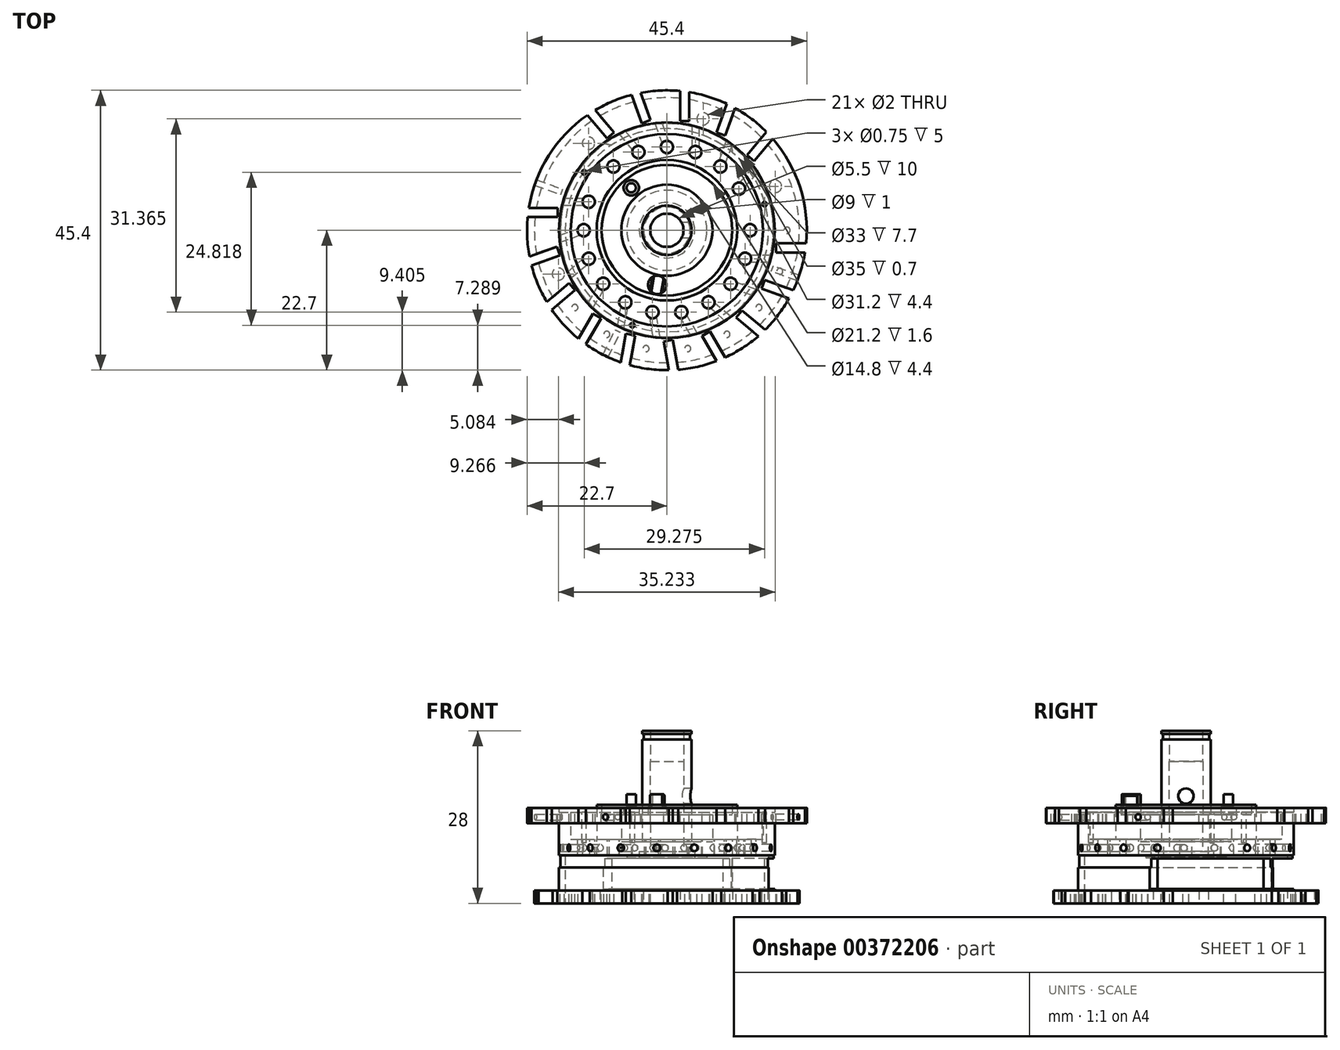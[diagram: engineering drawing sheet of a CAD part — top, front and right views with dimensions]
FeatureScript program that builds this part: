
annotation { "Feature Type Name" : "Feature", "Feature Type Description" : "" }
export const myFeature = defineFeature(function(context is Context, id is Id, definition is map)
    precondition{}
    {
        {
            var Q0;
            Q0=qCreatedBy(makeId("Front.planeOp"),FACE);
            var sketch = newSketch(context, id + "F0", { "sketchPlane" : qUnion([Q0])});
            skLineSegment(sketch, "E0", {"start": v(4, 20.6) * mm, "end": v(4, 20.1) * mm});
            skLineSegment(sketch, "E1", {"start": v(4, 20.1) * mm, "end": v(3.75, 20.1) * mm});
            skLineSegment(sketch, "E2", {"start": v(3.75, 20.1) * mm, "end": v(3.75, 19.2) * mm});
            skLineSegment(sketch, "E3", {"start": v(3.75, 19.2) * mm, "end": v(4, 19.2) * mm});
            skLineSegment(sketch, "E4", {"start": v(4, 19.2) * mm, "end": v(4, 2.6) * mm});
            skLineSegment(sketch, "E5", {"start": v(4, 2.6) * mm, "end": v(7.4, 2.6) * mm});
            skLineSegment(sketch, "E6", {"start": v(7.4, 2.6) * mm, "end": v(7.4, 7) * mm});
            skLineSegment(sketch, "E7", {"start": v(7.4, 7) * mm, "end": v(10.6, 7) * mm});
            skLineSegment(sketch, "E8", {"start": v(10.6, 7) * mm, "end": v(10.6, 8.6) * mm});
            skLineSegment(sketch, "E9", {"start": v(10.6, 8.6) * mm, "end": v(11.4, 8.6) * mm});
            skLineSegment(sketch, "E10", {"start": v(11.4, 8.6) * mm, "end": v(11.4, 3) * mm});
            skLineSegment(sketch, "E11", {"start": v(11.4, 3) * mm, "end": v(15.6, 3) * mm});
            skLineSegment(sketch, "E12", {"start": v(15.6, 3) * mm, "end": v(15.6, 7.4) * mm});
            skLineSegment(sketch, "E13", {"start": v(15.6, 7.4) * mm, "end": v(17.5, 7.4) * mm});
            skLineSegment(sketch, "E14", {"start": v(17.5, 7.4) * mm, "end": v(17.5, 8.1) * mm});
            skLineSegment(sketch, "E15", {"start": v(17.5, 8.1) * mm, "end": v(22.7, 8.1) * mm});
            skLineSegment(sketch, "E16", {"start": v(22.7, 8.1) * mm, "end": v(22.7, 5.6) * mm});
            skLineSegment(sketch, "E17", {"start": v(22.7, 5.6) * mm, "end": v(17.5, 5.6) * mm});
            skLineSegment(sketch, "E18", {"start": v(17.5, 5.6) * mm, "end": v(17.5, 0.4) * mm});
            skLineSegment(sketch, "E19", {"start": v(17.5, 0.4) * mm, "end": v(17.3, 0.4) * mm});
            skLineSegment(sketch, "E20", {"start": v(17.3, 0.4) * mm, "end": v(17.3, -1.6) * mm});
            skLineSegment(sketch, "E21", {"start": v(17.3, -1.6) * mm, "end": v(17.5, -1.6) * mm});
            skLineSegment(sketch, "E22", {"start": v(17.5, -1.6) * mm, "end": v(17.5, -5.3) * mm});
            skLineSegment(sketch, "E23", {"start": v(17.5, -5.3) * mm, "end": v(21.5, -5.3) * mm});
            skLineSegment(sketch, "E24", {"start": v(21.5, -5.3) * mm, "end": v(21.5, -7.4) * mm});
            skLineSegment(sketch, "E25", {"start": v(21.5, -7.4) * mm, "end": v(16.5, -7.4) * mm});
            skLineSegment(sketch, "E26", {"start": v(16.5, -7.4) * mm, "end": v(16.5, 0.3) * mm});
            skLineSegment(sketch, "E27", {"start": v(16.5, 0.3) * mm, "end": v(6.5, 0.3) * mm});
            skLineSegment(sketch, "E28", {"start": v(6.5, 0.3) * mm, "end": v(6.5, 0) * mm});
            skLineSegment(sketch, "E29", {"start": v(6.5, 0) * mm, "end": v(4.5, 0) * mm});
            skLineSegment(sketch, "E30", {"start": v(4.5, 0) * mm, "end": v(4.5, 1) * mm});
            skLineSegment(sketch, "E31", {"start": v(4.5, 1) * mm, "end": v(2.7, 1) * mm});
            skLineSegment(sketch, "E32", {"start": v(2.7, 1) * mm, "end": v(2.7, 5.6) * mm});
            skLineSegment(sketch, "E33", {"start": v(2.7, 5.6) * mm, "end": v(2.75, 5.6) * mm});
            skLineSegment(sketch, "E34", {"start": v(2.75, 5.6) * mm, "end": v(2.75, 15.6) * mm});
            skLineSegment(sketch, "E35", {"start": v(2.75, 15.6) * mm, "end": v(2.7, 15.6) * mm});
            skLineSegment(sketch, "E36", {"start": v(2.7, 15.6) * mm, "end": v(2.7, 20.6) * mm});
            skLineSegment(sketch, "E37", {"start": v(2.7, 20.6) * mm, "end": v(4, 20.6) * mm});
            skLineSegment(sketch, "E38", {"start": v(0, 0) * mm, "end": v(0, 20.6) * mm, "construction": true});
            skSolve(sketch);
        }
        {
            var Q0;
            Q0=makeQuery(id+"F0.imprint","IMPRINT",FACE,{"disambiguationData":[TD([[makeQuery(id+"F0.imprint","IMPRINT",EDGE,{"derivedFrom":sQuery(id+"F0.wireOp",EDGE,"E0")}),-1.0]])]});
            var Q1;
            Q1=sQuery(id+"F0.wireOp",EDGE,"E38");
            revolve(context, id + "F1", {"entities" : qUnion([Q0]), "axis" : qUnion([Q1]), "revolveType" : RevolveType.FULL});
        }
        {
            var Q0;
            Q0=makeQuery(id+"F1.opRevolve","SWEPT_FACE",FACE,{"disambiguationData":[OSD([sQuery(id+"F0.wireOp",EDGE,"E15")])]});
            var sketch = newSketch(context, id + "F2", { "sketchPlane" : qUnion([Q0])});
            skLineSegment(sketch, "E39.bottom", {"start": v(24.7, -2.13) * mm, "end": v(17.7, -2.13) * mm});
            skLineSegment(sketch, "E39.top", {"start": v(24.7, -3.63) * mm, "end": v(17.7, -3.63) * mm});
            skLineSegment(sketch, "E39.left", {"start": v(24.7, -2.13) * mm, "end": v(24.7, -3.63) * mm});
            skLineSegment(sketch, "E39.right", {"start": v(17.7, -2.13) * mm, "end": v(17.7, -3.63) * mm});
            skLineSegment(sketch, "E40", {"start": v(14.9, -4.63) * mm, "end": v(24.7, -4.63) * mm, "construction": true});
            skLineSegment(sketch, "E41", {"start": v(0, 0) * mm, "end": v(21.33, -7.76) * mm, "construction": true});
            skPoint(sketch, "E42", {"position": v(12.69, -4.62) * mm});
            skCircle(sketch, "E43", {"center": v(12.69, -4.62) * mm, "radius": 1 * mm});
            skLineSegment(sketch, "E44", {"start": v(14.9, -4.63) * mm, "end": v(13.69, -4.63) * mm, "construction": true});
            skSolve(sketch);
        }
        {
            var Q0;
            Q0=makeQuery(id+"F2.imprint","IMPRINT",FACE,{"disambiguationData":[TD([[makeQuery(id+"F2.imprint","IMPRINT",EDGE,{"derivedFrom":sQuery(id+"F2.wireOp",EDGE,"E43")}),1.0]])]});
            var Q1;
            {var subQ5=sQuery(id+"F2.wireOp",EDGE,"E39.right");Q1=makeQuery(id+"F2.imprint","IMPRINT",FACE,{"disambiguationData":[TD([[makeQuery(id+"F2.imprint","IMPRINT",EDGE,{"derivedFrom":subQ5}),1.0]])]});}
            extrude(context, id + "F3", {"entities" : qUnion([Q0, Q1]), "oppositeDirection" : true, "depth" : 16 * mm});
        }
        {
            var Q0;
            Q0=makeQuery(id+"F3.opExtrude","SWEPT_BODY",BODY,{"disambiguationData":[OSD([sQuery(id+"F0.wireOp",EDGE,"E15"),sQuery(id+"F0.wireOp",EDGE,"E16"),sQuery(id+"F2.wireOp",EDGE,"E39.bottom"),sQuery(id+"F2.wireOp",EDGE,"E39.top"),sQuery(id+"F2.wireOp",EDGE,"E39.right")])]});
            var Q1;
            Q1=makeQuery(id+"F3.opExtrude","SWEPT_BODY",BODY,{"disambiguationData":[OSD([sQuery(id+"F2.wireOp",EDGE,"E43")])]});
            var Q2;
            Q2=sQuery(id+"F0.wireOp",EDGE,"E38");
            circularPattern(context, id + "F4", {"entities" : qUnion([Q0, Q1]), "axis" : qUnion([Q2]), "angle" : 20 * degree, "instanceCount" : round(10), "oppositeDirection" : true, "computeTransformsWithoutBuiltin" : true});
        }
        {
            var Q0;
            Q0=makeQuery(id+"F3.opExtrude","SWEPT_BODY",BODY,{"disambiguationData":[OSD([sQuery(id+"F0.wireOp",EDGE,"E15"),sQuery(id+"F0.wireOp",EDGE,"E16"),sQuery(id+"F2.wireOp",EDGE,"E39.bottom"),sQuery(id+"F2.wireOp",EDGE,"E39.top"),sQuery(id+"F2.wireOp",EDGE,"E39.right")])]});
            var Q1;
            Q1=makeQuery(id+"F3.opExtrude","SWEPT_BODY",BODY,{"disambiguationData":[OSD([sQuery(id+"F2.wireOp",EDGE,"E43")])]});
            var Q2;
            Q2=sQuery(id+"F0.wireOp",EDGE,"E38");
            circularPattern(context, id + "F5", {"entities" : qUnion([Q0, Q1]), "axis" : qUnion([Q2]), "angle" : 50 * degree, "instanceCount" : round(2), "computeTransformsWithoutBuiltin" : true});
        }
        {
            var Q0;
            Q0=makeQuery(id+"F5.opPattern","COPY",BODY,{"derivedFrom":makeQuery(id+"F3.opExtrude","SWEPT_BODY",BODY,{"disambiguationData":[OSD([sQuery(id+"F2.wireOp",EDGE,"E43")])]}),"instanceName":"1"});
            var Q1;
            Q1=makeQuery(id+"F5.opPattern","COPY",BODY,{"derivedFrom":makeQuery(id+"F3.opExtrude","SWEPT_BODY",BODY,{"disambiguationData":[OSD([sQuery(id+"F0.wireOp",EDGE,"E15"),sQuery(id+"F0.wireOp",EDGE,"E16"),sQuery(id+"F2.wireOp",EDGE,"E39.bottom"),sQuery(id+"F2.wireOp",EDGE,"E39.top"),sQuery(id+"F2.wireOp",EDGE,"E39.right")])]}),"instanceName":"1"});
            var Q2;
            Q2=sQuery(id+"F0.wireOp",EDGE,"E38");
            circularPattern(context, id + "F6", {"entities" : qUnion([Q0, Q1]), "axis" : qUnion([Q2]), "angle" : 20 * degree, "instanceCount" : round(5), "computeTransformsWithoutBuiltin" : true});
        }
        {
            var Q0;
            Q0=makeQuery(id+"F6.opPattern","COPY",BODY,{"derivedFrom":makeQuery(id+"F5.opPattern","COPY",BODY,{"derivedFrom":makeQuery(id+"F3.opExtrude","SWEPT_BODY",BODY,{"disambiguationData":[OSD([sQuery(id+"F2.wireOp",EDGE,"E43")])]}),"instanceName":"1"}),"instanceName":"4"});
            var Q1;
            Q1=sQuery(id+"F0.wireOp",EDGE,"E38");
            transform(context, id + "F7", {"entities" : qUnion([Q0]), "transformType" : TransformType.ROTATION, "transformAxis" : qUnion([Q1]), "angle" : 20 * degree, "makeCopy" : true});
        }
        {
            var Q0;
            Q0=makeQuery(id+"F3.opExtrude","SWEPT_BODY",BODY,{"disambiguationData":[OSD([sQuery(id+"F0.wireOp",EDGE,"E15"),sQuery(id+"F0.wireOp",EDGE,"E16"),sQuery(id+"F2.wireOp",EDGE,"E39.bottom"),sQuery(id+"F2.wireOp",EDGE,"E39.top"),sQuery(id+"F2.wireOp",EDGE,"E39.right")])]});
            var Q1;
            Q1=makeQuery(id+"F3.opExtrude","SWEPT_BODY",BODY,{"disambiguationData":[OSD([sQuery(id+"F2.wireOp",EDGE,"E43")])]});
            var Q2;
            Q2=makeQuery(id+"F4.opPattern","COPY",BODY,{"derivedFrom":makeQuery(id+"F3.opExtrude","SWEPT_BODY",BODY,{"disambiguationData":[OSD([sQuery(id+"F0.wireOp",EDGE,"E15"),sQuery(id+"F0.wireOp",EDGE,"E16"),sQuery(id+"F2.wireOp",EDGE,"E39.bottom"),sQuery(id+"F2.wireOp",EDGE,"E39.top"),sQuery(id+"F2.wireOp",EDGE,"E39.right")])]}),"instanceName":"1"});
            var Q3;
            Q3=makeQuery(id+"F4.opPattern","COPY",BODY,{"derivedFrom":makeQuery(id+"F3.opExtrude","SWEPT_BODY",BODY,{"disambiguationData":[OSD([sQuery(id+"F2.wireOp",EDGE,"E43")])]}),"instanceName":"1"});
            var Q4;
            Q4=makeQuery(id+"F4.opPattern","COPY",BODY,{"derivedFrom":makeQuery(id+"F3.opExtrude","SWEPT_BODY",BODY,{"disambiguationData":[OSD([sQuery(id+"F0.wireOp",EDGE,"E15"),sQuery(id+"F0.wireOp",EDGE,"E16"),sQuery(id+"F2.wireOp",EDGE,"E39.bottom"),sQuery(id+"F2.wireOp",EDGE,"E39.top"),sQuery(id+"F2.wireOp",EDGE,"E39.right")])]}),"instanceName":"2"});
            var Q5;
            Q5=makeQuery(id+"F4.opPattern","COPY",BODY,{"derivedFrom":makeQuery(id+"F3.opExtrude","SWEPT_BODY",BODY,{"disambiguationData":[OSD([sQuery(id+"F2.wireOp",EDGE,"E43")])]}),"instanceName":"2"});
            var Q6;
            Q6=makeQuery(id+"F4.opPattern","COPY",BODY,{"derivedFrom":makeQuery(id+"F3.opExtrude","SWEPT_BODY",BODY,{"disambiguationData":[OSD([sQuery(id+"F0.wireOp",EDGE,"E15"),sQuery(id+"F0.wireOp",EDGE,"E16"),sQuery(id+"F2.wireOp",EDGE,"E39.bottom"),sQuery(id+"F2.wireOp",EDGE,"E39.top"),sQuery(id+"F2.wireOp",EDGE,"E39.right")])]}),"instanceName":"3"});
            var Q7;
            Q7=makeQuery(id+"F4.opPattern","COPY",BODY,{"derivedFrom":makeQuery(id+"F3.opExtrude","SWEPT_BODY",BODY,{"disambiguationData":[OSD([sQuery(id+"F2.wireOp",EDGE,"E43")])]}),"instanceName":"3"});
            var Q8;
            Q8=makeQuery(id+"F4.opPattern","COPY",BODY,{"derivedFrom":makeQuery(id+"F3.opExtrude","SWEPT_BODY",BODY,{"disambiguationData":[OSD([sQuery(id+"F0.wireOp",EDGE,"E15"),sQuery(id+"F0.wireOp",EDGE,"E16"),sQuery(id+"F2.wireOp",EDGE,"E39.bottom"),sQuery(id+"F2.wireOp",EDGE,"E39.top"),sQuery(id+"F2.wireOp",EDGE,"E39.right")])]}),"instanceName":"4"});
            var Q9;
            Q9=makeQuery(id+"F4.opPattern","COPY",BODY,{"derivedFrom":makeQuery(id+"F3.opExtrude","SWEPT_BODY",BODY,{"disambiguationData":[OSD([sQuery(id+"F2.wireOp",EDGE,"E43")])]}),"instanceName":"4"});
            var Q10;
            Q10=makeQuery(id+"F4.opPattern","COPY",BODY,{"derivedFrom":makeQuery(id+"F3.opExtrude","SWEPT_BODY",BODY,{"disambiguationData":[OSD([sQuery(id+"F0.wireOp",EDGE,"E15"),sQuery(id+"F0.wireOp",EDGE,"E16"),sQuery(id+"F2.wireOp",EDGE,"E39.bottom"),sQuery(id+"F2.wireOp",EDGE,"E39.top"),sQuery(id+"F2.wireOp",EDGE,"E39.right")])]}),"instanceName":"5"});
            var Q11;
            Q11=makeQuery(id+"F4.opPattern","COPY",BODY,{"derivedFrom":makeQuery(id+"F3.opExtrude","SWEPT_BODY",BODY,{"disambiguationData":[OSD([sQuery(id+"F2.wireOp",EDGE,"E43")])]}),"instanceName":"5"});
            var Q12;
            Q12=makeQuery(id+"F4.opPattern","COPY",BODY,{"derivedFrom":makeQuery(id+"F3.opExtrude","SWEPT_BODY",BODY,{"disambiguationData":[OSD([sQuery(id+"F0.wireOp",EDGE,"E15"),sQuery(id+"F0.wireOp",EDGE,"E16"),sQuery(id+"F2.wireOp",EDGE,"E39.bottom"),sQuery(id+"F2.wireOp",EDGE,"E39.top"),sQuery(id+"F2.wireOp",EDGE,"E39.right")])]}),"instanceName":"6"});
            var Q13;
            Q13=makeQuery(id+"F4.opPattern","COPY",BODY,{"derivedFrom":makeQuery(id+"F3.opExtrude","SWEPT_BODY",BODY,{"disambiguationData":[OSD([sQuery(id+"F2.wireOp",EDGE,"E43")])]}),"instanceName":"6"});
            var Q14;
            Q14=makeQuery(id+"F4.opPattern","COPY",BODY,{"derivedFrom":makeQuery(id+"F3.opExtrude","SWEPT_BODY",BODY,{"disambiguationData":[OSD([sQuery(id+"F0.wireOp",EDGE,"E15"),sQuery(id+"F0.wireOp",EDGE,"E16"),sQuery(id+"F2.wireOp",EDGE,"E39.bottom"),sQuery(id+"F2.wireOp",EDGE,"E39.top"),sQuery(id+"F2.wireOp",EDGE,"E39.right")])]}),"instanceName":"7"});
            var Q15;
            Q15=makeQuery(id+"F4.opPattern","COPY",BODY,{"derivedFrom":makeQuery(id+"F3.opExtrude","SWEPT_BODY",BODY,{"disambiguationData":[OSD([sQuery(id+"F2.wireOp",EDGE,"E43")])]}),"instanceName":"7"});
            var Q16;
            Q16=makeQuery(id+"F4.opPattern","COPY",BODY,{"derivedFrom":makeQuery(id+"F3.opExtrude","SWEPT_BODY",BODY,{"disambiguationData":[OSD([sQuery(id+"F0.wireOp",EDGE,"E15"),sQuery(id+"F0.wireOp",EDGE,"E16"),sQuery(id+"F2.wireOp",EDGE,"E39.bottom"),sQuery(id+"F2.wireOp",EDGE,"E39.top"),sQuery(id+"F2.wireOp",EDGE,"E39.right")])]}),"instanceName":"8"});
            var Q17;
            Q17=makeQuery(id+"F4.opPattern","COPY",BODY,{"derivedFrom":makeQuery(id+"F3.opExtrude","SWEPT_BODY",BODY,{"disambiguationData":[OSD([sQuery(id+"F2.wireOp",EDGE,"E43")])]}),"instanceName":"8"});
            var Q18;
            Q18=makeQuery(id+"F4.opPattern","COPY",BODY,{"derivedFrom":makeQuery(id+"F3.opExtrude","SWEPT_BODY",BODY,{"disambiguationData":[OSD([sQuery(id+"F0.wireOp",EDGE,"E15"),sQuery(id+"F0.wireOp",EDGE,"E16"),sQuery(id+"F2.wireOp",EDGE,"E39.bottom"),sQuery(id+"F2.wireOp",EDGE,"E39.top"),sQuery(id+"F2.wireOp",EDGE,"E39.right")])]}),"instanceName":"9"});
            var Q19;
            Q19=makeQuery(id+"F4.opPattern","COPY",BODY,{"derivedFrom":makeQuery(id+"F3.opExtrude","SWEPT_BODY",BODY,{"disambiguationData":[OSD([sQuery(id+"F2.wireOp",EDGE,"E43")])]}),"instanceName":"9"});
            var Q20;
            Q20=makeQuery(id+"F5.opPattern","COPY",BODY,{"derivedFrom":makeQuery(id+"F3.opExtrude","SWEPT_BODY",BODY,{"disambiguationData":[OSD([sQuery(id+"F0.wireOp",EDGE,"E15"),sQuery(id+"F0.wireOp",EDGE,"E16"),sQuery(id+"F2.wireOp",EDGE,"E39.bottom"),sQuery(id+"F2.wireOp",EDGE,"E39.top"),sQuery(id+"F2.wireOp",EDGE,"E39.right")])]}),"instanceName":"1"});
            var Q21;
            Q21=makeQuery(id+"F5.opPattern","COPY",BODY,{"derivedFrom":makeQuery(id+"F3.opExtrude","SWEPT_BODY",BODY,{"disambiguationData":[OSD([sQuery(id+"F2.wireOp",EDGE,"E43")])]}),"instanceName":"1"});
            var Q22;
            Q22=makeQuery(id+"F6.opPattern","COPY",BODY,{"derivedFrom":makeQuery(id+"F5.opPattern","COPY",BODY,{"derivedFrom":makeQuery(id+"F3.opExtrude","SWEPT_BODY",BODY,{"disambiguationData":[OSD([sQuery(id+"F0.wireOp",EDGE,"E15"),sQuery(id+"F0.wireOp",EDGE,"E16"),sQuery(id+"F2.wireOp",EDGE,"E39.bottom"),sQuery(id+"F2.wireOp",EDGE,"E39.top"),sQuery(id+"F2.wireOp",EDGE,"E39.right")])]}),"instanceName":"1"}),"instanceName":"1"});
            var Q23;
            Q23=makeQuery(id+"F6.opPattern","COPY",BODY,{"derivedFrom":makeQuery(id+"F5.opPattern","COPY",BODY,{"derivedFrom":makeQuery(id+"F3.opExtrude","SWEPT_BODY",BODY,{"disambiguationData":[OSD([sQuery(id+"F2.wireOp",EDGE,"E43")])]}),"instanceName":"1"}),"instanceName":"1"});
            var Q24;
            Q24=makeQuery(id+"F6.opPattern","COPY",BODY,{"derivedFrom":makeQuery(id+"F5.opPattern","COPY",BODY,{"derivedFrom":makeQuery(id+"F3.opExtrude","SWEPT_BODY",BODY,{"disambiguationData":[OSD([sQuery(id+"F0.wireOp",EDGE,"E15"),sQuery(id+"F0.wireOp",EDGE,"E16"),sQuery(id+"F2.wireOp",EDGE,"E39.bottom"),sQuery(id+"F2.wireOp",EDGE,"E39.top"),sQuery(id+"F2.wireOp",EDGE,"E39.right")])]}),"instanceName":"1"}),"instanceName":"2"});
            var Q25;
            Q25=makeQuery(id+"F6.opPattern","COPY",BODY,{"derivedFrom":makeQuery(id+"F5.opPattern","COPY",BODY,{"derivedFrom":makeQuery(id+"F3.opExtrude","SWEPT_BODY",BODY,{"disambiguationData":[OSD([sQuery(id+"F2.wireOp",EDGE,"E43")])]}),"instanceName":"1"}),"instanceName":"2"});
            var Q26;
            Q26=makeQuery(id+"F6.opPattern","COPY",BODY,{"derivedFrom":makeQuery(id+"F5.opPattern","COPY",BODY,{"derivedFrom":makeQuery(id+"F3.opExtrude","SWEPT_BODY",BODY,{"disambiguationData":[OSD([sQuery(id+"F0.wireOp",EDGE,"E15"),sQuery(id+"F0.wireOp",EDGE,"E16"),sQuery(id+"F2.wireOp",EDGE,"E39.bottom"),sQuery(id+"F2.wireOp",EDGE,"E39.top"),sQuery(id+"F2.wireOp",EDGE,"E39.right")])]}),"instanceName":"1"}),"instanceName":"3"});
            var Q27;
            Q27=makeQuery(id+"F6.opPattern","COPY",BODY,{"derivedFrom":makeQuery(id+"F5.opPattern","COPY",BODY,{"derivedFrom":makeQuery(id+"F3.opExtrude","SWEPT_BODY",BODY,{"disambiguationData":[OSD([sQuery(id+"F2.wireOp",EDGE,"E43")])]}),"instanceName":"1"}),"instanceName":"3"});
            var Q28;
            Q28=makeQuery(id+"F6.opPattern","COPY",BODY,{"derivedFrom":makeQuery(id+"F5.opPattern","COPY",BODY,{"derivedFrom":makeQuery(id+"F3.opExtrude","SWEPT_BODY",BODY,{"disambiguationData":[OSD([sQuery(id+"F0.wireOp",EDGE,"E15"),sQuery(id+"F0.wireOp",EDGE,"E16"),sQuery(id+"F2.wireOp",EDGE,"E39.bottom"),sQuery(id+"F2.wireOp",EDGE,"E39.top"),sQuery(id+"F2.wireOp",EDGE,"E39.right")])]}),"instanceName":"1"}),"instanceName":"4"});
            var Q29;
            Q29=makeQuery(id+"F6.opPattern","COPY",BODY,{"derivedFrom":makeQuery(id+"F5.opPattern","COPY",BODY,{"derivedFrom":makeQuery(id+"F3.opExtrude","SWEPT_BODY",BODY,{"disambiguationData":[OSD([sQuery(id+"F2.wireOp",EDGE,"E43")])]}),"instanceName":"1"}),"instanceName":"4"});
            var Q30;
            Q30=makeQuery(id+"F6.opPattern","COPY",BODY,{"derivedFrom":makeQuery(id+"F5.opPattern","COPY",BODY,{"derivedFrom":makeQuery(id+"F3.opExtrude","SWEPT_BODY",BODY,{"disambiguationData":[OSD([sQuery(id+"F0.wireOp",EDGE,"E15"),sQuery(id+"F0.wireOp",EDGE,"E16"),sQuery(id+"F2.wireOp",EDGE,"E39.bottom"),sQuery(id+"F2.wireOp",EDGE,"E39.top"),sQuery(id+"F2.wireOp",EDGE,"E39.right")])]}),"instanceName":"1"}),"instanceName":"5"});
            var Q31;
            Q31=makeQuery(id+"F6.opPattern","COPY",BODY,{"derivedFrom":makeQuery(id+"F5.opPattern","COPY",BODY,{"derivedFrom":makeQuery(id+"F3.opExtrude","SWEPT_BODY",BODY,{"disambiguationData":[OSD([sQuery(id+"F2.wireOp",EDGE,"E43")])]}),"instanceName":"1"}),"instanceName":"5"});
            var Q32;
            Q32=makeQuery(id+"F7.opPattern","COPY",BODY,{"derivedFrom":makeQuery(id+"F6.opPattern","COPY",BODY,{"derivedFrom":makeQuery(id+"F5.opPattern","COPY",BODY,{"derivedFrom":makeQuery(id+"F3.opExtrude","SWEPT_BODY",BODY,{"disambiguationData":[OSD([sQuery(id+"F2.wireOp",EDGE,"E43")])]}),"instanceName":"1"}),"instanceName":"4"}),"instanceName":"1"});
            var Q33;
            Q33=makeQuery(id+"F1.opRevolve","SWEPT_BODY",BODY,{"disambiguationData":[OSD([sQuery(id+"F0.wireOp",EDGE,"E0"),sQuery(id+"F0.wireOp",EDGE,"E1"),sQuery(id+"F0.wireOp",EDGE,"E2"),sQuery(id+"F0.wireOp",EDGE,"E3"),sQuery(id+"F0.wireOp",EDGE,"E4"),sQuery(id+"F0.wireOp",EDGE,"E5"),sQuery(id+"F0.wireOp",EDGE,"E6"),sQuery(id+"F0.wireOp",EDGE,"E7"),sQuery(id+"F0.wireOp",EDGE,"E8"),sQuery(id+"F0.wireOp",EDGE,"E9"),sQuery(id+"F0.wireOp",EDGE,"E10"),sQuery(id+"F0.wireOp",EDGE,"E11"),sQuery(id+"F0.wireOp",EDGE,"E12"),sQuery(id+"F0.wireOp",EDGE,"E13"),sQuery(id+"F0.wireOp",EDGE,"E14"),sQuery(id+"F0.wireOp",EDGE,"E15"),sQuery(id+"F0.wireOp",EDGE,"E16"),sQuery(id+"F0.wireOp",EDGE,"E17"),sQuery(id+"F0.wireOp",EDGE,"E18"),sQuery(id+"F0.wireOp",EDGE,"E19"),sQuery(id+"F0.wireOp",EDGE,"E20"),sQuery(id+"F0.wireOp",EDGE,"E21"),sQuery(id+"F0.wireOp",EDGE,"E22"),sQuery(id+"F0.wireOp",EDGE,"E23"),sQuery(id+"F0.wireOp",EDGE,"E24"),sQuery(id+"F0.wireOp",EDGE,"E25"),sQuery(id+"F0.wireOp",EDGE,"E26"),sQuery(id+"F0.wireOp",EDGE,"E27"),sQuery(id+"F0.wireOp",EDGE,"E28"),sQuery(id+"F0.wireOp",EDGE,"E29"),sQuery(id+"F0.wireOp",EDGE,"E30"),sQuery(id+"F0.wireOp",EDGE,"E31"),sQuery(id+"F0.wireOp",EDGE,"E32"),sQuery(id+"F0.wireOp",EDGE,"E33"),sQuery(id+"F0.wireOp",EDGE,"E34"),sQuery(id+"F0.wireOp",EDGE,"E35"),sQuery(id+"F0.wireOp",EDGE,"E36"),sQuery(id+"F0.wireOp",EDGE,"E37")])]});
            booleanBodies(context, id + "F8", {"operationType" : BooleanOperationType.SUBTRACTION, "tools" : qUnion([Q0, Q1, Q2, Q3, Q4, Q5, Q6, Q7, Q8, Q9, Q10, Q11, Q12, Q13, Q14, Q15, Q16, Q17, Q18, Q19, Q20, Q21, Q22, Q23, Q24, Q25, Q26, Q27, Q28, Q29, Q30, Q31, Q32]), "targets" : qUnion([Q33])});
        }
        {
            var Q0;
            Q0=makeQuery(id+"F1.opRevolve","SWEPT_FACE",FACE,{"disambiguationData":[OSD([sQuery(id+"F0.wireOp",EDGE,"E9")])]});
            cPlane(context, id + "F9", {"entities" : qUnion([Q0]), "cplaneType" : CPlaneType.OFFSET, "offset" : 7 * mm, "oppositeDirection" : true, "width" : 150 * mm, "height" : 150 * mm});
        }
        {
            var Q0;
            Q0=qCreatedBy(id+"F9.planeOp",FACE);
            var sketch = newSketch(context, id + "F10", { "sketchPlane" : qUnion([Q0])});
            skLineSegment(sketch, "E45", {"start": v(23.53, -4.63) * mm, "end": v(13.53, -4.63) * mm, "construction": true});
            skLineSegment(sketch, "E46", {"start": v(0, 0) * mm, "end": v(12.69, -4.62) * mm, "construction": true});
            skCircle(sketch, "E47", {"center": v(12.69, -4.62) * mm, "radius": 1 * mm, "construction": true});
            skLineSegment(sketch, "E48.bottom", {"start": v(13.53, -4.63) * mm, "end": v(23.53, -4.63) * mm});
            skLineSegment(sketch, "E48.top", {"start": v(13.53, -4.08) * mm, "end": v(23.53, -4.08) * mm});
            skLineSegment(sketch, "E48.left", {"start": v(13.53, -4.63) * mm, "end": v(13.53, -4.08) * mm});
            skLineSegment(sketch, "E48.right", {"start": v(23.53, -4.63) * mm, "end": v(23.53, -4.08) * mm});
            skSolve(sketch);
        }
        {
            var Q0;
            Q0=makeQuery(id+"F10.imprint","IMPRINT",FACE,{"disambiguationData":[TD([[makeQuery(id+"F10.imprint","IMPRINT",EDGE,{"derivedFrom":sQuery(id+"F10.wireOp",EDGE,"E48.bottom")}),1.0]])]});
            var Q1;
            Q1=sQuery(id+"F10.wireOp",EDGE,"E48.bottom");
            revolve(context, id + "F11", {"entities" : qUnion([Q0]), "axis" : qUnion([Q1]), "revolveType" : RevolveType.FULL});
        }
        {
            var Q0;
            Q0=makeQuery(id+"F11.opRevolve","SWEPT_BODY",BODY,{"disambiguationData":[OSD([sQuery(id+"F10.wireOp",EDGE,"E48.bottom"),sQuery(id+"F10.wireOp",EDGE,"E48.top"),sQuery(id+"F10.wireOp",EDGE,"E48.left"),sQuery(id+"F10.wireOp",EDGE,"E48.right")])]});
            var Q1;
            Q1=sQuery(id+"F0.wireOp",EDGE,"E38");
            circularPattern(context, id + "F12", {"entities" : qUnion([Q0]), "axis" : qUnion([Q1]), "angle" : 20 * degree, "instanceCount" : round(10), "oppositeDirection" : true, "computeTransformsWithoutBuiltin" : true});
        }
        {
            var Q0;
            Q0=makeQuery(id+"F11.opRevolve","SWEPT_BODY",BODY,{"disambiguationData":[OSD([sQuery(id+"F10.wireOp",EDGE,"E48.bottom"),sQuery(id+"F10.wireOp",EDGE,"E48.top"),sQuery(id+"F10.wireOp",EDGE,"E48.left"),sQuery(id+"F10.wireOp",EDGE,"E48.right")])]});
            var Q1;
            Q1=sQuery(id+"F0.wireOp",EDGE,"E38");
            circularPattern(context, id + "F13", {"entities" : qUnion([Q0]), "axis" : qUnion([Q1]), "angle" : 50 * degree, "instanceCount" : 2, "computeTransformsWithoutBuiltin" : true});
        }
        {
            var Q0;
            Q0=makeQuery(id+"F13.opPattern","COPY",BODY,{"derivedFrom":makeQuery(id+"F11.opRevolve","SWEPT_BODY",BODY,{"disambiguationData":[OSD([sQuery(id+"F10.wireOp",EDGE,"E48.bottom"),sQuery(id+"F10.wireOp",EDGE,"E48.top"),sQuery(id+"F10.wireOp",EDGE,"E48.left"),sQuery(id+"F10.wireOp",EDGE,"E48.right")])]}),"instanceName":"1"});
            var Q1;
            Q1=sQuery(id+"F0.wireOp",EDGE,"E38");
            circularPattern(context, id + "F14", {"entities" : qUnion([Q0]), "axis" : qUnion([Q1]), "angle" : 20 * degree, "instanceCount" : round(5), "computeTransformsWithoutBuiltin" : true});
        }
        {
            var Q0;
            Q0=makeQuery(id+"F11.opRevolve","SWEPT_BODY",BODY,{"disambiguationData":[OSD([sQuery(id+"F10.wireOp",EDGE,"E48.bottom"),sQuery(id+"F10.wireOp",EDGE,"E48.top"),sQuery(id+"F10.wireOp",EDGE,"E48.left"),sQuery(id+"F10.wireOp",EDGE,"E48.right")])]});
            var Q1;
            Q1=makeQuery(id+"F12.opPattern","COPY",BODY,{"derivedFrom":makeQuery(id+"F11.opRevolve","SWEPT_BODY",BODY,{"disambiguationData":[OSD([sQuery(id+"F10.wireOp",EDGE,"E48.bottom"),sQuery(id+"F10.wireOp",EDGE,"E48.top"),sQuery(id+"F10.wireOp",EDGE,"E48.left"),sQuery(id+"F10.wireOp",EDGE,"E48.right")])]}),"instanceName":"1"});
            var Q2;
            Q2=makeQuery(id+"F12.opPattern","COPY",BODY,{"derivedFrom":makeQuery(id+"F11.opRevolve","SWEPT_BODY",BODY,{"disambiguationData":[OSD([sQuery(id+"F10.wireOp",EDGE,"E48.bottom"),sQuery(id+"F10.wireOp",EDGE,"E48.top"),sQuery(id+"F10.wireOp",EDGE,"E48.left"),sQuery(id+"F10.wireOp",EDGE,"E48.right")])]}),"instanceName":"2"});
            var Q3;
            Q3=makeQuery(id+"F12.opPattern","COPY",BODY,{"derivedFrom":makeQuery(id+"F11.opRevolve","SWEPT_BODY",BODY,{"disambiguationData":[OSD([sQuery(id+"F10.wireOp",EDGE,"E48.bottom"),sQuery(id+"F10.wireOp",EDGE,"E48.top"),sQuery(id+"F10.wireOp",EDGE,"E48.left"),sQuery(id+"F10.wireOp",EDGE,"E48.right")])]}),"instanceName":"3"});
            var Q4;
            Q4=makeQuery(id+"F12.opPattern","COPY",BODY,{"derivedFrom":makeQuery(id+"F11.opRevolve","SWEPT_BODY",BODY,{"disambiguationData":[OSD([sQuery(id+"F10.wireOp",EDGE,"E48.bottom"),sQuery(id+"F10.wireOp",EDGE,"E48.top"),sQuery(id+"F10.wireOp",EDGE,"E48.left"),sQuery(id+"F10.wireOp",EDGE,"E48.right")])]}),"instanceName":"4"});
            var Q5;
            Q5=makeQuery(id+"F12.opPattern","COPY",BODY,{"derivedFrom":makeQuery(id+"F11.opRevolve","SWEPT_BODY",BODY,{"disambiguationData":[OSD([sQuery(id+"F10.wireOp",EDGE,"E48.bottom"),sQuery(id+"F10.wireOp",EDGE,"E48.top"),sQuery(id+"F10.wireOp",EDGE,"E48.left"),sQuery(id+"F10.wireOp",EDGE,"E48.right")])]}),"instanceName":"5"});
            var Q6;
            Q6=makeQuery(id+"F12.opPattern","COPY",BODY,{"derivedFrom":makeQuery(id+"F11.opRevolve","SWEPT_BODY",BODY,{"disambiguationData":[OSD([sQuery(id+"F10.wireOp",EDGE,"E48.bottom"),sQuery(id+"F10.wireOp",EDGE,"E48.top"),sQuery(id+"F10.wireOp",EDGE,"E48.left"),sQuery(id+"F10.wireOp",EDGE,"E48.right")])]}),"instanceName":"6"});
            var Q7;
            Q7=makeQuery(id+"F12.opPattern","COPY",BODY,{"derivedFrom":makeQuery(id+"F11.opRevolve","SWEPT_BODY",BODY,{"disambiguationData":[OSD([sQuery(id+"F10.wireOp",EDGE,"E48.bottom"),sQuery(id+"F10.wireOp",EDGE,"E48.top"),sQuery(id+"F10.wireOp",EDGE,"E48.left"),sQuery(id+"F10.wireOp",EDGE,"E48.right")])]}),"instanceName":"7"});
            var Q8;
            Q8=makeQuery(id+"F12.opPattern","COPY",BODY,{"derivedFrom":makeQuery(id+"F11.opRevolve","SWEPT_BODY",BODY,{"disambiguationData":[OSD([sQuery(id+"F10.wireOp",EDGE,"E48.bottom"),sQuery(id+"F10.wireOp",EDGE,"E48.top"),sQuery(id+"F10.wireOp",EDGE,"E48.left"),sQuery(id+"F10.wireOp",EDGE,"E48.right")])]}),"instanceName":"8"});
            var Q9;
            Q9=makeQuery(id+"F12.opPattern","COPY",BODY,{"derivedFrom":makeQuery(id+"F11.opRevolve","SWEPT_BODY",BODY,{"disambiguationData":[OSD([sQuery(id+"F10.wireOp",EDGE,"E48.bottom"),sQuery(id+"F10.wireOp",EDGE,"E48.top"),sQuery(id+"F10.wireOp",EDGE,"E48.left"),sQuery(id+"F10.wireOp",EDGE,"E48.right")])]}),"instanceName":"9"});
            var Q10;
            Q10=makeQuery(id+"F13.opPattern","COPY",BODY,{"derivedFrom":makeQuery(id+"F11.opRevolve","SWEPT_BODY",BODY,{"disambiguationData":[OSD([sQuery(id+"F10.wireOp",EDGE,"E48.bottom"),sQuery(id+"F10.wireOp",EDGE,"E48.top"),sQuery(id+"F10.wireOp",EDGE,"E48.left"),sQuery(id+"F10.wireOp",EDGE,"E48.right")])]}),"instanceName":"1"});
            var Q11;
            Q11=makeQuery(id+"F14.opPattern","COPY",BODY,{"derivedFrom":makeQuery(id+"F13.opPattern","COPY",BODY,{"derivedFrom":makeQuery(id+"F11.opRevolve","SWEPT_BODY",BODY,{"disambiguationData":[OSD([sQuery(id+"F10.wireOp",EDGE,"E48.bottom"),sQuery(id+"F10.wireOp",EDGE,"E48.top"),sQuery(id+"F10.wireOp",EDGE,"E48.left"),sQuery(id+"F10.wireOp",EDGE,"E48.right")])]}),"instanceName":"1"}),"instanceName":"1"});
            var Q12;
            Q12=makeQuery(id+"F14.opPattern","COPY",BODY,{"derivedFrom":makeQuery(id+"F13.opPattern","COPY",BODY,{"derivedFrom":makeQuery(id+"F11.opRevolve","SWEPT_BODY",BODY,{"disambiguationData":[OSD([sQuery(id+"F10.wireOp",EDGE,"E48.bottom"),sQuery(id+"F10.wireOp",EDGE,"E48.top"),sQuery(id+"F10.wireOp",EDGE,"E48.left"),sQuery(id+"F10.wireOp",EDGE,"E48.right")])]}),"instanceName":"1"}),"instanceName":"2"});
            var Q13;
            Q13=makeQuery(id+"F14.opPattern","COPY",BODY,{"derivedFrom":makeQuery(id+"F13.opPattern","COPY",BODY,{"derivedFrom":makeQuery(id+"F11.opRevolve","SWEPT_BODY",BODY,{"disambiguationData":[OSD([sQuery(id+"F10.wireOp",EDGE,"E48.bottom"),sQuery(id+"F10.wireOp",EDGE,"E48.top"),sQuery(id+"F10.wireOp",EDGE,"E48.left"),sQuery(id+"F10.wireOp",EDGE,"E48.right")])]}),"instanceName":"1"}),"instanceName":"3"});
            var Q14;
            Q14=makeQuery(id+"F14.opPattern","COPY",BODY,{"derivedFrom":makeQuery(id+"F13.opPattern","COPY",BODY,{"derivedFrom":makeQuery(id+"F11.opRevolve","SWEPT_BODY",BODY,{"disambiguationData":[OSD([sQuery(id+"F10.wireOp",EDGE,"E48.bottom"),sQuery(id+"F10.wireOp",EDGE,"E48.top"),sQuery(id+"F10.wireOp",EDGE,"E48.left"),sQuery(id+"F10.wireOp",EDGE,"E48.right")])]}),"instanceName":"1"}),"instanceName":"4"});
            var Q15;
            Q15=makeQuery(id+"F14.opPattern","COPY",BODY,{"derivedFrom":makeQuery(id+"F13.opPattern","COPY",BODY,{"derivedFrom":makeQuery(id+"F11.opRevolve","SWEPT_BODY",BODY,{"disambiguationData":[OSD([sQuery(id+"F10.wireOp",EDGE,"E48.bottom"),sQuery(id+"F10.wireOp",EDGE,"E48.top"),sQuery(id+"F10.wireOp",EDGE,"E48.left"),sQuery(id+"F10.wireOp",EDGE,"E48.right")])]}),"instanceName":"1"}),"instanceName":"5"});
            var Q16;
            Q16=makeQuery(id+"F1.opRevolve","SWEPT_BODY",BODY,{"disambiguationData":[OSD([sQuery(id+"F0.wireOp",EDGE,"E0"),sQuery(id+"F0.wireOp",EDGE,"E1"),sQuery(id+"F0.wireOp",EDGE,"E2"),sQuery(id+"F0.wireOp",EDGE,"E3"),sQuery(id+"F0.wireOp",EDGE,"E4"),sQuery(id+"F0.wireOp",EDGE,"E5"),sQuery(id+"F0.wireOp",EDGE,"E6"),sQuery(id+"F0.wireOp",EDGE,"E7"),sQuery(id+"F0.wireOp",EDGE,"E8"),sQuery(id+"F0.wireOp",EDGE,"E9"),sQuery(id+"F0.wireOp",EDGE,"E10"),sQuery(id+"F0.wireOp",EDGE,"E11"),sQuery(id+"F0.wireOp",EDGE,"E12"),sQuery(id+"F0.wireOp",EDGE,"E13"),sQuery(id+"F0.wireOp",EDGE,"E14"),sQuery(id+"F0.wireOp",EDGE,"E15"),sQuery(id+"F0.wireOp",EDGE,"E16"),sQuery(id+"F0.wireOp",EDGE,"E17"),sQuery(id+"F0.wireOp",EDGE,"E18"),sQuery(id+"F0.wireOp",EDGE,"E19"),sQuery(id+"F0.wireOp",EDGE,"E20"),sQuery(id+"F0.wireOp",EDGE,"E21"),sQuery(id+"F0.wireOp",EDGE,"E22"),sQuery(id+"F0.wireOp",EDGE,"E23"),sQuery(id+"F0.wireOp",EDGE,"E24"),sQuery(id+"F0.wireOp",EDGE,"E25"),sQuery(id+"F0.wireOp",EDGE,"E26"),sQuery(id+"F0.wireOp",EDGE,"E27"),sQuery(id+"F0.wireOp",EDGE,"E28"),sQuery(id+"F0.wireOp",EDGE,"E29"),sQuery(id+"F0.wireOp",EDGE,"E30"),sQuery(id+"F0.wireOp",EDGE,"E31"),sQuery(id+"F0.wireOp",EDGE,"E32"),sQuery(id+"F0.wireOp",EDGE,"E33"),sQuery(id+"F0.wireOp",EDGE,"E34"),sQuery(id+"F0.wireOp",EDGE,"E35"),sQuery(id+"F0.wireOp",EDGE,"E36"),sQuery(id+"F0.wireOp",EDGE,"E37")])]});
            booleanBodies(context, id + "F15", {"operationType" : BooleanOperationType.SUBTRACTION, "tools" : qUnion([Q0, Q1, Q2, Q3, Q4, Q5, Q6, Q7, Q8, Q9, Q10, Q11, Q12, Q13, Q14, Q15]), "targets" : qUnion([Q16])});
        }
        {
            var Q0;
            Q0=makeQuery(id+"F1.opRevolve","SWEPT_FACE",FACE,{"disambiguationData":[OSD([sQuery(id+"F0.wireOp",EDGE,"E11")])]});
            var sketch = newSketch(context, id + "F16", { "sketchPlane" : qUnion([Q0])});
            skCircle(sketch, "E49", {"center": v(13.5, 0) * mm, "radius": 1 * mm});
            skSolve(sketch);
        }
        {
            var Q0;
            Q0=makeQuery(id+"F16.imprint","IMPRINT",FACE,{"disambiguationData":[TD([[makeQuery(id+"F16.imprint","IMPRINT",EDGE,{"derivedFrom":sQuery(id+"F16.wireOp",EDGE,"E49")}),1.0]])]});
            extrude(context, id + "F17", {"entities" : qUnion([Q0]), "operationType" : NewBodyOperationType.REMOVE, "oppositeDirection" : true, "depth" : 25 * mm});
        }
        {
            var Q0;
            Q0=makeQuery(id+"F1.opRevolve","SWEPT_FACE",FACE,{"disambiguationData":[OSD([sQuery(id+"F0.wireOp",EDGE,"E7")])]});
            var sketch = newSketch(context, id + "F18", { "sketchPlane" : qUnion([Q0])});
            skCircle(sketch, "E50", {"center": v(-1.56, -8.86) * mm, "radius": 1.5 * mm});
            skCircle(sketch, "E51", {"center": v(-5.79, 6.9) * mm, "radius": 1.25 * mm});
            skLineSegment(sketch, "E52", {"start": v(-5.79, 6.9) * mm, "end": v(0, 0) * mm, "construction": true});
            skLineSegment(sketch, "E53", {"start": v(0, 0) * mm, "end": v(-1.56, -8.86) * mm, "construction": true});
            skSolve(sketch);
        }
        {
            var Q0;
            {Q0=qUnion([makeQuery(id+"F18.imprint","IMPRINT",FACE,{"disambiguationData":[TD([[makeQuery(id+"F18.imprint","IMPRINT",EDGE,{"derivedFrom":sQuery(id+"F18.wireOp",EDGE,"E50")}),1.0]])]}),makeQuery(id+"F18.imprint","IMPRINT",FACE,{"disambiguationData":[TD([[makeQuery(id+"F18.imprint","IMPRINT",EDGE,{"derivedFrom":sQuery(id+"F18.wireOp",EDGE,"E51")}),1.0]])]})]);}
            extrude(context, id + "F19", {"entities" : qUnion([Q0]), "operationType" : NewBodyOperationType.ADD, "depth" : 1.2 * mm});
        }
        {
            var Q0;
            Q0=makeQuery(id+"F19.opExtrude","CAP_FACE",FACE,{"disambiguationData":[OSD([sQuery(id+"F18.wireOp",EDGE,"E51")])],"isStart":false});
            var sketch = newSketch(context, id + "F20", { "sketchPlane" : qUnion([Q0])});
            skCircle(sketch, "E54", {"center": v(-5.79, 6.9) * mm, "radius": 0.75 * mm});
            skSolve(sketch);
        }
        {
            var Q0;
            Q0=makeQuery(id+"F20.imprint","IMPRINT",FACE,{"disambiguationData":[TD([[makeQuery(id+"F20.imprint","IMPRINT",EDGE,{"derivedFrom":sQuery(id+"F20.wireOp",EDGE,"E54")}),1.0]])]});
            extrude(context, id + "F21", {"entities" : qUnion([Q0]), "operationType" : NewBodyOperationType.ADD, "depth" : 2.1 * mm});
        }
        {
            var Q0;
            Q0=makeQuery(id+"F19.opExtrude","CAP_FACE",FACE,{"disambiguationData":[OSD([sQuery(id+"F18.wireOp",EDGE,"E50")])],"isStart":false});
            var sketch = newSketch(context, id + "F22", { "sketchPlane" : qUnion([Q0])});
            skLineSegment(sketch, "E55", {"start": v(0, 0) * mm, "end": v(-1.82, -10.34) * mm, "construction": true});
            skLineSegment(sketch, "E56", {"start": v(-2.35, -7.59) * mm, "end": v(-2.74, -9.8) * mm});
            skLineSegment(sketch, "E57", {"start": v(-0.38, -7.94) * mm, "end": v(-0.77, -10.14) * mm});
            skSolve(sketch);
        }
        {
            var Q0;
            {var subQ2=sQuery(id+"F22.wireOp",EDGE,"E56");Q0=makeQuery(id+"F22.imprint","IMPRINT",FACE,{"disambiguationData":[TD([[makeQuery(id+"F22.imprint","IMPRINT",EDGE,{"derivedFrom":subQ2}),1.0]])]});}
            extrude(context, id + "F23", {"entities" : qUnion([Q0]), "operationType" : NewBodyOperationType.ADD, "depth" : 2.1 * mm});
        }
        {
            var Q0;
            Q0=makeQuery(id+"F23.opExtrude","CAP_EDGE",EDGE,{"disambiguationData":[OSD([sQuery(id+"F22.wireOp",EDGE,"E56")])],"isStart":false});
            var Q1;
            Q1=makeQuery(id+"F23.opExtrude","CAP_EDGE",EDGE,{"disambiguationData":[OSD([sQuery(id+"F22.wireOp",EDGE,"E57")])],"isStart":false});
            chamfer(context, id + "F24", {"entities" : qUnion([Q0, Q1]), "chamferType" : ChamferType.OFFSET_ANGLE, "width" : 0.25 * mm, "oppositeDirection" : true, "angle" : 30 * degree, "tangentPropagation" : true});
        }
        {
            var Q0;
            Q0=makeQuery(id+"F1.opRevolve","SWEPT_FACE",FACE,{"disambiguationData":[OSD([sQuery(id+"F0.wireOp",EDGE,"E13")])]});
            var sketch = newSketch(context, id + "F25", { "sketchPlane" : qUnion([Q0])});
            skCircle(sketch, "E58", {"center": v(15.84, 4.24) * mm, "radius": 0.38 * mm});
            skLineSegment(sketch, "E59", {"start": v(0, 0) * mm, "end": v(15.84, 4.24) * mm, "construction": true});
            skCircle(sketch, "E60", {"center": v(0, 0) * mm, "radius": 16.4 * mm, "construction": true});
            skLineSegment(sketch, "E61", {"start": v(0, 0) * mm, "end": v(-5.6, -15.41) * mm, "construction": true});
            skLineSegment(sketch, "E62", {"start": v(-5.6, -15.41) * mm, "end": v(0, 0) * mm, "construction": true});
            skLineSegment(sketch, "E63", {"start": v(0, 0) * mm, "end": v(-13.43, 9.4) * mm, "construction": true});
            skCircle(sketch, "E64", {"center": v(-13.43, 9.4) * mm, "radius": 0.38 * mm});
            skCircle(sketch, "E65", {"center": v(-5.6, -15.41) * mm, "radius": 0.38 * mm});
            skSolve(sketch);
        }
        {
            var Q0;
            Q0=makeQuery(id+"F25.imprint","IMPRINT",FACE,{"disambiguationData":[TD([[makeQuery(id+"F25.imprint","IMPRINT",EDGE,{"derivedFrom":sQuery(id+"F25.wireOp",EDGE,"E58")}),1.0]])]});
            var Q1;
            Q1=makeQuery(id+"F25.imprint","IMPRINT",FACE,{"disambiguationData":[TD([[makeQuery(id+"F25.imprint","IMPRINT",EDGE,{"derivedFrom":sQuery(id+"F25.wireOp",EDGE,"E65")}),1.0]])]});
            var Q2;
            Q2=makeQuery(id+"F25.imprint","IMPRINT",FACE,{"disambiguationData":[TD([[makeQuery(id+"F25.imprint","IMPRINT",EDGE,{"derivedFrom":sQuery(id+"F25.wireOp",EDGE,"E64")}),1.0]])]});
            var Q3;
            Q3=sQuery(id+"F25.wireOp",EDGE,"E58");
            extrude(context, id + "F26", {"entities" : qUnion([Q0, Q1, Q2]), "surfaceEntities" : qUnion([Q3]), "oppositeDirection" : true, "depth" : 5 * mm});
        }
        {
            var Q0;
            Q0=makeQuery(id+"F26.opExtrude","SWEPT_BODY",BODY,{"disambiguationData":[OSD([sQuery(id+"F25.wireOp",EDGE,"E58")])]});
            var Q1;
            Q1=makeQuery(id+"F26.opExtrude","SWEPT_BODY",BODY,{"disambiguationData":[OSD([sQuery(id+"F25.wireOp",EDGE,"E64")])]});
            var Q2;
            Q2=makeQuery(id+"F26.opExtrude","SWEPT_BODY",BODY,{"disambiguationData":[OSD([sQuery(id+"F25.wireOp",EDGE,"E65")])]});
            var Q3;
            Q3=makeQuery(id+"F1.opRevolve","SWEPT_BODY",BODY,{"disambiguationData":[OSD([sQuery(id+"F0.wireOp",EDGE,"E0"),sQuery(id+"F0.wireOp",EDGE,"E1"),sQuery(id+"F0.wireOp",EDGE,"E2"),sQuery(id+"F0.wireOp",EDGE,"E3"),sQuery(id+"F0.wireOp",EDGE,"E4"),sQuery(id+"F0.wireOp",EDGE,"E5"),sQuery(id+"F0.wireOp",EDGE,"E6"),sQuery(id+"F0.wireOp",EDGE,"E7"),sQuery(id+"F0.wireOp",EDGE,"E8"),sQuery(id+"F0.wireOp",EDGE,"E9"),sQuery(id+"F0.wireOp",EDGE,"E10"),sQuery(id+"F0.wireOp",EDGE,"E11"),sQuery(id+"F0.wireOp",EDGE,"E12"),sQuery(id+"F0.wireOp",EDGE,"E13"),sQuery(id+"F0.wireOp",EDGE,"E14"),sQuery(id+"F0.wireOp",EDGE,"E15"),sQuery(id+"F0.wireOp",EDGE,"E16"),sQuery(id+"F0.wireOp",EDGE,"E17"),sQuery(id+"F0.wireOp",EDGE,"E18"),sQuery(id+"F0.wireOp",EDGE,"E19"),sQuery(id+"F0.wireOp",EDGE,"E20"),sQuery(id+"F0.wireOp",EDGE,"E21"),sQuery(id+"F0.wireOp",EDGE,"E22"),sQuery(id+"F0.wireOp",EDGE,"E23"),sQuery(id+"F0.wireOp",EDGE,"E24"),sQuery(id+"F0.wireOp",EDGE,"E25"),sQuery(id+"F0.wireOp",EDGE,"E26"),sQuery(id+"F0.wireOp",EDGE,"E27"),sQuery(id+"F0.wireOp",EDGE,"E28"),sQuery(id+"F0.wireOp",EDGE,"E29"),sQuery(id+"F0.wireOp",EDGE,"E30"),sQuery(id+"F0.wireOp",EDGE,"E31"),sQuery(id+"F0.wireOp",EDGE,"E32"),sQuery(id+"F0.wireOp",EDGE,"E33"),sQuery(id+"F0.wireOp",EDGE,"E34"),sQuery(id+"F0.wireOp",EDGE,"E35"),sQuery(id+"F0.wireOp",EDGE,"E36"),sQuery(id+"F0.wireOp",EDGE,"E37")])]});
            booleanBodies(context, id + "F27", {"operationType" : BooleanOperationType.SUBTRACTION, "tools" : qUnion([Q0, Q1, Q2]), "targets" : qUnion([Q3])});
        }
        {
            var Q0;
            Q0=makeQuery(id+"F1.opRevolve","SWEPT_FACE",FACE,{"disambiguationData":[OSD([sQuery(id+"F0.wireOp",EDGE,"E9")])]});
            cPlane(context, id + "F28", {"entities" : qUnion([Q0]), "cplaneType" : CPlaneType.OFFSET, "offset" : 2 * mm, "oppositeDirection" : true, "width" : 150 * mm, "height" : 150 * mm});
        }
        {
            var Q0;
            Q0=qCreatedBy(id+"F28.planeOp",FACE);
            var sketch = newSketch(context, id + "F29", { "sketchPlane" : qUnion([Q0])});
            skLineSegment(sketch, "E66", {"start": v(0, 0) * mm, "end": v(21.61, -7.87) * mm, "construction": true});
            skLineSegment(sketch, "E67", {"start": v(21.61, -7.87) * mm, "end": v(21.78, -7.42) * mm});
            skLineSegment(sketch, "E68", {"start": v(21.78, -7.42) * mm, "end": v(17.26, -5.78) * mm});
            skLineSegment(sketch, "E69", {"start": v(17.26, -5.78) * mm, "end": v(17.1, -6.22) * mm});
            skLineSegment(sketch, "E70", {"start": v(17.1, -6.22) * mm, "end": v(21.61, -7.87) * mm});
            skSolve(sketch);
        }
        {
            var Q0;
            Q0=makeQuery(id+"F29.imprint","IMPRINT",FACE,{"disambiguationData":[TD([[makeQuery(id+"F29.imprint","IMPRINT",EDGE,{"derivedFrom":sQuery(id+"F29.wireOp",EDGE,"E67")}),1.0]])]});
            var Q1;
            Q1=sQuery(id+"F29.wireOp",EDGE,"E66");
            revolve(context, id + "F30", {"entities" : qUnion([Q0]), "axis" : qUnion([Q1]), "revolveType" : RevolveType.FULL});
        }
        {
            var Q0;
            Q0=makeQuery(id+"F30.opRevolve","SWEPT_BODY",BODY,{"disambiguationData":[OSD([sQuery(id+"F29.wireOp",EDGE,"E67"),sQuery(id+"F29.wireOp",EDGE,"E68"),sQuery(id+"F29.wireOp",EDGE,"E69"),sQuery(id+"F29.wireOp",EDGE,"E70")])]});
            var Q1;
            Q1=sQuery(id+"F0.wireOp",EDGE,"E38");
            circularPattern(context, id + "F31", {"entities" : qUnion([Q0]), "axis" : qUnion([Q1]), "angle" : 96 * degree, "instanceCount" : 2, "oppositeDirection" : true, "computeTransformsWithoutBuiltin" : true});
        }
        {
            var Q0;
            Q0=makeQuery(id+"F31.opPattern","COPY",BODY,{"derivedFrom":makeQuery(id+"F30.opRevolve","SWEPT_BODY",BODY,{"disambiguationData":[OSD([sQuery(id+"F29.wireOp",EDGE,"E67"),sQuery(id+"F29.wireOp",EDGE,"E68"),sQuery(id+"F29.wireOp",EDGE,"E69"),sQuery(id+"F29.wireOp",EDGE,"E70")])]}),"instanceName":"1"});
            var Q1;
            Q1=sQuery(id+"F0.wireOp",EDGE,"E38");
            circularPattern(context, id + "F32", {"entities" : qUnion([Q0]), "axis" : qUnion([Q1]), "angle" : 84 * degree, "instanceCount" : 2, "oppositeDirection" : true, "computeTransformsWithoutBuiltin" : true});
        }
        {
            var Q0;
            Q0=makeQuery(id+"F30.opRevolve","SWEPT_BODY",BODY,{"disambiguationData":[OSD([sQuery(id+"F29.wireOp",EDGE,"E67"),sQuery(id+"F29.wireOp",EDGE,"E68"),sQuery(id+"F29.wireOp",EDGE,"E69"),sQuery(id+"F29.wireOp",EDGE,"E70")])]});
            var Q1;
            Q1=makeQuery(id+"F31.opPattern","COPY",BODY,{"derivedFrom":makeQuery(id+"F30.opRevolve","SWEPT_BODY",BODY,{"disambiguationData":[OSD([sQuery(id+"F29.wireOp",EDGE,"E67"),sQuery(id+"F29.wireOp",EDGE,"E68"),sQuery(id+"F29.wireOp",EDGE,"E69"),sQuery(id+"F29.wireOp",EDGE,"E70")])]}),"instanceName":"1"});
            var Q2;
            Q2=makeQuery(id+"F32.opPattern","COPY",BODY,{"derivedFrom":makeQuery(id+"F31.opPattern","COPY",BODY,{"derivedFrom":makeQuery(id+"F30.opRevolve","SWEPT_BODY",BODY,{"disambiguationData":[OSD([sQuery(id+"F29.wireOp",EDGE,"E67"),sQuery(id+"F29.wireOp",EDGE,"E68"),sQuery(id+"F29.wireOp",EDGE,"E69"),sQuery(id+"F29.wireOp",EDGE,"E70")])]}),"instanceName":"1"}),"instanceName":"1"});
            var Q3;
            Q3=makeQuery(id+"F1.opRevolve","SWEPT_BODY",BODY,{"disambiguationData":[OSD([sQuery(id+"F0.wireOp",EDGE,"E0"),sQuery(id+"F0.wireOp",EDGE,"E1"),sQuery(id+"F0.wireOp",EDGE,"E2"),sQuery(id+"F0.wireOp",EDGE,"E3"),sQuery(id+"F0.wireOp",EDGE,"E4"),sQuery(id+"F0.wireOp",EDGE,"E5"),sQuery(id+"F0.wireOp",EDGE,"E6"),sQuery(id+"F0.wireOp",EDGE,"E7"),sQuery(id+"F0.wireOp",EDGE,"E8"),sQuery(id+"F0.wireOp",EDGE,"E9"),sQuery(id+"F0.wireOp",EDGE,"E10"),sQuery(id+"F0.wireOp",EDGE,"E11"),sQuery(id+"F0.wireOp",EDGE,"E12"),sQuery(id+"F0.wireOp",EDGE,"E13"),sQuery(id+"F0.wireOp",EDGE,"E14"),sQuery(id+"F0.wireOp",EDGE,"E15"),sQuery(id+"F0.wireOp",EDGE,"E16"),sQuery(id+"F0.wireOp",EDGE,"E17"),sQuery(id+"F0.wireOp",EDGE,"E18"),sQuery(id+"F0.wireOp",EDGE,"E19"),sQuery(id+"F0.wireOp",EDGE,"E20"),sQuery(id+"F0.wireOp",EDGE,"E21"),sQuery(id+"F0.wireOp",EDGE,"E22"),sQuery(id+"F0.wireOp",EDGE,"E23"),sQuery(id+"F0.wireOp",EDGE,"E24"),sQuery(id+"F0.wireOp",EDGE,"E25"),sQuery(id+"F0.wireOp",EDGE,"E26"),sQuery(id+"F0.wireOp",EDGE,"E27"),sQuery(id+"F0.wireOp",EDGE,"E28"),sQuery(id+"F0.wireOp",EDGE,"E29"),sQuery(id+"F0.wireOp",EDGE,"E30"),sQuery(id+"F0.wireOp",EDGE,"E31"),sQuery(id+"F0.wireOp",EDGE,"E32"),sQuery(id+"F0.wireOp",EDGE,"E33"),sQuery(id+"F0.wireOp",EDGE,"E34"),sQuery(id+"F0.wireOp",EDGE,"E35"),sQuery(id+"F0.wireOp",EDGE,"E36"),sQuery(id+"F0.wireOp",EDGE,"E37")])]});
            booleanBodies(context, id + "F33", {"operationType" : BooleanOperationType.SUBTRACTION, "tools" : qUnion([Q0, Q1, Q2]), "targets" : qUnion([Q3])});
        }
        {
            var Q0;
            Q0=qCreatedBy(makeId("Right.planeOp"),FACE);
            var sketch = newSketch(context, id + "F34", { "sketchPlane" : qUnion([Q0])});
            skCircle(sketch, "E71", {"center": v(0, 10) * mm, "radius": 1.25 * mm});
            skSolve(sketch);
        }
        {
            var Q0;
            Q0=makeQuery(id+"F34.imprint","IMPRINT",FACE,{"disambiguationData":[TD([[makeQuery(id+"F34.imprint","IMPRINT",EDGE,{"derivedFrom":sQuery(id+"F34.wireOp",EDGE,"E71")}),1.0]])]});
            extrude(context, id + "F35", {"entities" : qUnion([Q0]), "operationType" : NewBodyOperationType.REMOVE, "depth" : 5 * mm});
        }
        {
            var Q0;
            Q0=makeQuery(id+"F1.opRevolve","SWEPT_FACE",FACE,{"disambiguationData":[OSD([sQuery(id+"F0.wireOp",EDGE,"E23")])]});
            var sketch = newSketch(context, id + "F36", { "sketchPlane" : qUnion([Q0])});
            skCircle(sketch, "E72", {"center": v(19.5, 0) * mm, "radius": 0.5 * mm});
            skCircle(sketch, "E73.1.0", {"center": v(18.32, -6.67) * mm, "radius": 0.5 * mm});
            skCircle(sketch, "E73.2.0", {"center": v(14.94, -12.53) * mm, "radius": 0.5 * mm});
            skCircle(sketch, "E73.3.0", {"center": v(9.75, -16.89) * mm, "radius": 0.5 * mm});
            skCircle(sketch, "E73.4.0", {"center": v(3.39, -19.2) * mm, "radius": 0.5 * mm});
            skCircle(sketch, "E73.5.0", {"center": v(-3.39, -19.2) * mm, "radius": 0.5 * mm});
            skCircle(sketch, "E73.6.0", {"center": v(-9.75, -16.89) * mm, "radius": 0.5 * mm});
            skCircle(sketch, "E73.7.0", {"center": v(-14.94, -12.53) * mm, "radius": 0.5 * mm});
            skPoint(sketch, "E73.center", {"position": v(0, 0) * mm});
            skLineSegment(sketch, "E73.anchor1", {"start": v(0, 0) * mm, "end": v(19.5, 0) * mm, "construction": true});
            skLineSegment(sketch, "E73.anchor2", {"start": v(0, 0) * mm, "end": v(-14.94, -12.53) * mm, "construction": true});
            skSolve(sketch);
        }
        {
            var Q0;
            {Q0=qUnion([makeQuery(id+"F36.imprint","IMPRINT",FACE,{"disambiguationData":[TD([[makeQuery(id+"F36.imprint","IMPRINT",EDGE,{"derivedFrom":sQuery(id+"F36.wireOp",EDGE,"E72")}),1.0]])]}),makeQuery(id+"F36.imprint","IMPRINT",FACE,{"disambiguationData":[TD([[makeQuery(id+"F36.imprint","IMPRINT",EDGE,{"derivedFrom":sQuery(id+"F36.wireOp",EDGE,"E73.1.0")}),1.0]])]}),makeQuery(id+"F36.imprint","IMPRINT",FACE,{"disambiguationData":[TD([[makeQuery(id+"F36.imprint","IMPRINT",EDGE,{"derivedFrom":sQuery(id+"F36.wireOp",EDGE,"E73.2.0")}),1.0]])]}),makeQuery(id+"F36.imprint","IMPRINT",FACE,{"disambiguationData":[TD([[makeQuery(id+"F36.imprint","IMPRINT",EDGE,{"derivedFrom":sQuery(id+"F36.wireOp",EDGE,"E73.3.0")}),1.0]])]}),makeQuery(id+"F36.imprint","IMPRINT",FACE,{"disambiguationData":[TD([[makeQuery(id+"F36.imprint","IMPRINT",EDGE,{"derivedFrom":sQuery(id+"F36.wireOp",EDGE,"E73.4.0")}),1.0]])]}),makeQuery(id+"F36.imprint","IMPRINT",FACE,{"disambiguationData":[TD([[makeQuery(id+"F36.imprint","IMPRINT",EDGE,{"derivedFrom":sQuery(id+"F36.wireOp",EDGE,"E73.5.0")}),1.0]])]}),makeQuery(id+"F36.imprint","IMPRINT",FACE,{"disambiguationData":[TD([[makeQuery(id+"F36.imprint","IMPRINT",EDGE,{"derivedFrom":sQuery(id+"F36.wireOp",EDGE,"E73.6.0")}),1.0]])]}),makeQuery(id+"F36.imprint","IMPRINT",FACE,{"disambiguationData":[TD([[makeQuery(id+"F36.imprint","IMPRINT",EDGE,{"derivedFrom":sQuery(id+"F36.wireOp",EDGE,"E73.7.0")}),1.0]])]})]);}
            extrude(context, id + "F37", {"entities" : qUnion([Q0]), "operationType" : NewBodyOperationType.REMOVE, "oppositeDirection" : true, "depth" : 2.5 * mm});
        }
        {
            var Q0;
            Q0=makeQuery(id+"F1.opRevolve","SWEPT_FACE",FACE,{"disambiguationData":[OSD([sQuery(id+"F0.wireOp",EDGE,"E23")])]});
            var sketch = newSketch(context, id + "F38", { "sketchPlane" : qUnion([Q0])});
            skLineSegment(sketch, "E74", {"start": v(0, 0) * mm, "end": v(17.62, 7.12) * mm, "construction": true});
            skCircle(sketch, "E75", {"center": v(17.62, 7.12) * mm, "radius": 1 * mm});
            skCircle(sketch, "E76.1.0", {"center": v(5.87, 18.07) * mm, "radius": 1 * mm});
            skPoint(sketch, "E76.center", {"position": v(0, 0) * mm});
            skLineSegment(sketch, "E76.anchor2", {"start": v(0, 0) * mm, "end": v(5.87, 18.07) * mm, "construction": true});
            skCircle(sketch, "E77.1.0", {"center": v(-12.71, 14.12) * mm, "radius": 1 * mm});
            skLineSegment(sketch, "E77.anchor2", {"start": v(0, 0) * mm, "end": v(-12.71, 14.12) * mm, "construction": true});
            skCircle(sketch, "E78.1.0", {"center": v(-17.62, -7.12) * mm, "radius": 1 * mm});
            skLineSegment(sketch, "E78.anchor2", {"start": v(0, 0) * mm, "end": v(-17.62, -7.12) * mm, "construction": true});
            skSolve(sketch);
        }
        {
            var Q0;
            {Q0=qUnion([makeQuery(id+"F38.imprint","IMPRINT",FACE,{"disambiguationData":[TD([[makeQuery(id+"F38.imprint","IMPRINT",EDGE,{"derivedFrom":sQuery(id+"F38.wireOp",EDGE,"E75")}),1.0]])]}),makeQuery(id+"F38.imprint","IMPRINT",FACE,{"disambiguationData":[TD([[makeQuery(id+"F38.imprint","IMPRINT",EDGE,{"derivedFrom":sQuery(id+"F38.wireOp",EDGE,"E76.1.0")}),1.0]])]}),makeQuery(id+"F38.imprint","IMPRINT",FACE,{"disambiguationData":[TD([[makeQuery(id+"F38.imprint","IMPRINT",EDGE,{"derivedFrom":sQuery(id+"F38.wireOp",EDGE,"E77.1.0")}),1.0]])]}),makeQuery(id+"F38.imprint","IMPRINT",FACE,{"disambiguationData":[TD([[makeQuery(id+"F38.imprint","IMPRINT",EDGE,{"derivedFrom":sQuery(id+"F38.wireOp",EDGE,"E78.1.0")}),1.0]])]})]);}
            extrude(context, id + "F39", {"entities" : qUnion([Q0]), "operationType" : NewBodyOperationType.REMOVE, "oppositeDirection" : true, "depth" : 2.5 * mm});
        }
        {
            var Q0;
            Q0=makeQuery(id+"F1.opRevolve","SWEPT_FACE",FACE,{"disambiguationData":[OSD([sQuery(id+"F0.wireOp",EDGE,"E23")])]});
            cPlane(context, id + "F40", {"entities" : qUnion([Q0]), "cplaneType" : CPlaneType.OFFSET, "offset" : 0.2 * mm, "width" : 150 * mm, "height" : 150 * mm});
        }
        {
            var Q0;
            Q0=qCreatedBy(id+"F40.planeOp",FACE);
            var sketch = newSketch(context, id + "F41", { "sketchPlane" : qUnion([Q0])});
            skLineSegment(sketch, "E79", {"start": v(0, 0) * mm, "end": v(2.2, 62.93) * mm, "construction": true});
            skLineSegment(sketch, "E80", {"start": v(0, 0) * mm, "end": v(60.82, 16.3) * mm, "construction": true});
            skLineSegment(sketch, "E81", {"start": v(2.2, 62.93) * mm, "end": v(0.2, 63) * mm, "construction": true});
            skCircle(sketch, "E82", {"center": v(0.2, 63) * mm, "radius": 50 * mm});
            skLineSegment(sketch, "E83", {"start": v(60.82, 16.3) * mm, "end": v(60.3, 18.23) * mm, "construction": true});
            skCircle(sketch, "E84", {"center": v(60.3, 18.23) * mm, "radius": 50 * mm});
            skSolve(sketch);
        }
        {
            var Q0;
            {var subQ0=sQuery(id+"F41.wireOp",EDGE,"E84");var subQ1=sQuery(id+"F41.wireOp",EDGE,"E82");var subQ3=makeQuery(id+"F41.imprint","INTERSECT",VERTEX,{"disambiguationData":[OD(0.0)],"derivedFrom":[subQ1,subQ0]});var subQ5=makeQuery(id+"F41.imprint","IMPRINT",EDGE,{"disambiguationData":[TD([[subQ3,-1.0]])],"derivedFrom":subQ1});Q0=qUnion([makeQuery(id+"F41.imprint","IMPRINT",FACE,{"disambiguationData":[TD([[makeQuery(id+"F41.imprint","IMPRINT",EDGE,{"disambiguationData":[TD([[subQ3,1.0]])],"derivedFrom":subQ1}),1.0]])]}),makeQuery(id+"F41.imprint","IMPRINT",FACE,{"disambiguationData":[TD([[subQ5,-1.0]])]}),makeQuery(id+"F41.imprint","IMPRINT",FACE,{"disambiguationData":[TD([[subQ5,1.0]])]})]);}
            extrude(context, id + "F42", {"entities" : qUnion([Q0]), "operationType" : NewBodyOperationType.REMOVE, "depth" : 5 * mm});
        }
    });
